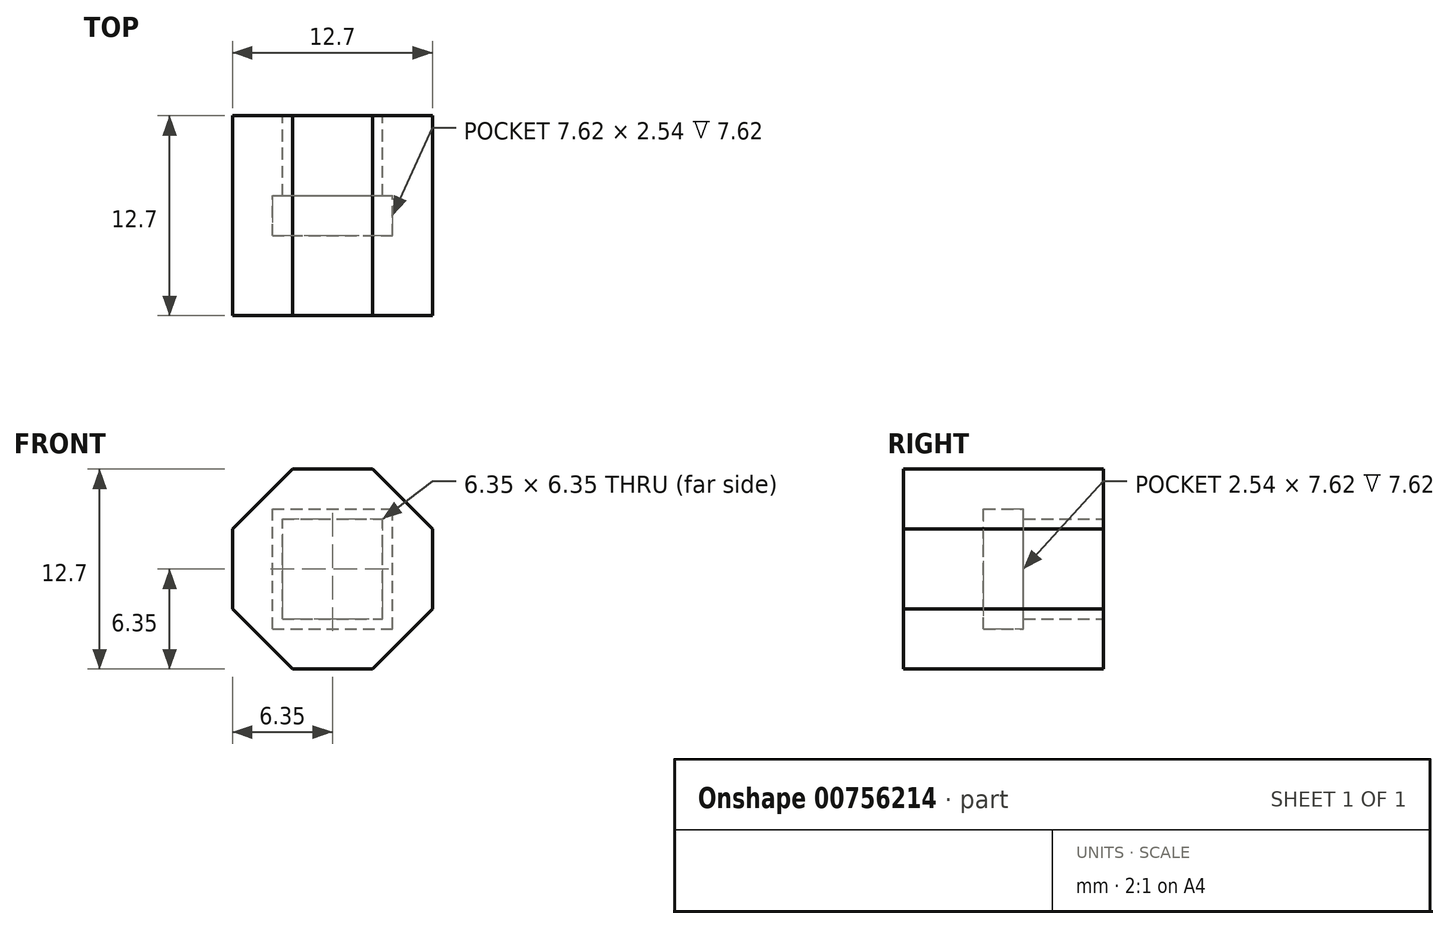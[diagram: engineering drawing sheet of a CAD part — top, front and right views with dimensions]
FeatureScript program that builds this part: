
annotation { "Feature Type Name" : "Feature", "Feature Type Description" : "" }
export const myFeature = defineFeature(function(context is Context, id is Id, definition is map)
    precondition{}
    {
        {
            var Q0;
            Q0=qCreatedBy(makeId("Front.planeOp"),FACE);
            var sketch = newSketch(context, id + "F0", { "sketchPlane" : qUnion([Q0])});
            skLineSegment(sketch, "E0.bottom", {"start": v(-6.35, -6.35) * mm, "end": v(6.35, -6.35) * mm});
            skLineSegment(sketch, "E0.top", {"start": v(-6.35, 6.35) * mm, "end": v(6.35, 6.35) * mm});
            skLineSegment(sketch, "E0.left", {"start": v(-6.35, -6.35) * mm, "end": v(-6.35, 6.35) * mm});
            skLineSegment(sketch, "E0.right", {"start": v(6.35, -6.35) * mm, "end": v(6.35, 6.35) * mm});
            skPoint(sketch, "E0.middle", {"position": v(0, 0) * mm});
            skLineSegment(sketch, "E1.bottom", {"start": v(-3.8, -3.81) * mm, "end": v(3.81, -3.81) * mm});
            skLineSegment(sketch, "E1.top", {"start": v(-3.81, 3.81) * mm, "end": v(3.8, 3.81) * mm});
            skLineSegment(sketch, "E1.left", {"start": v(-3.8, -3.81) * mm, "end": v(-3.81, 3.8) * mm});
            skLineSegment(sketch, "E1.right", {"start": v(3.81, -3.81) * mm, "end": v(3.8, 3.81) * mm});
            skLineSegment(sketch, "E2.bottom", {"start": v(-3.17, -3.18) * mm, "end": v(3.18, -3.18) * mm});
            skLineSegment(sketch, "E2.top", {"start": v(-3.18, 3.18) * mm, "end": v(3.17, 3.18) * mm});
            skLineSegment(sketch, "E2.left", {"start": v(-3.17, -3.18) * mm, "end": v(-3.18, 3.18) * mm});
            skLineSegment(sketch, "E2.right", {"start": v(3.18, -3.18) * mm, "end": v(3.17, 3.18) * mm});
            skSolve(sketch);
        }
        {
            var Q0;
            Q0=qSketchRegion(id+"F0",true);
            var Q1;
            Q1=makeQuery(id+"F0.imprint","IMPRINT",FACE,{"disambiguationData":[TD([[makeQuery(id+"F0.imprint","IMPRINT",EDGE,{"derivedFrom":sQuery(id+"F0.wireOp",EDGE,"E1.bottom")}),1.0]])]});
            var Q2;
            Q2=makeQuery(id+"F0.imprint","IMPRINT",FACE,{"disambiguationData":[TD([[makeQuery(id+"F0.imprint","IMPRINT",EDGE,{"derivedFrom":sQuery(id+"F0.wireOp",EDGE,"E2.bottom")}),1.0]])]});
            extrude(context, id + "F1", {"entities" : qUnion([Q0, Q1, Q2]), "depth" : 12.7 * mm, "offsetDistance" : 25.4 * mm});
        }
        {
            var Q0;
            Q0=makeQuery(id+"F0.imprint","IMPRINT",FACE,{"disambiguationData":[TD([[makeQuery(id+"F0.imprint","IMPRINT",EDGE,{"derivedFrom":sQuery(id+"F0.wireOp",EDGE,"E2.bottom")}),1.0]])]});
            extrude(context, id + "F2", {"entities" : qUnion([Q0]), "operationType" : NewBodyOperationType.REMOVE, "depth" : 7.62 * mm, "offsetDistance" : 25.4 * mm});
        }
        {
            var Q0;
            Q0=makeQuery(id+"F0.imprint","IMPRINT",FACE,{"disambiguationData":[TD([[makeQuery(id+"F0.imprint","IMPRINT",EDGE,{"derivedFrom":sQuery(id+"F0.wireOp",EDGE,"E1.bottom")}),1.0]])]});
            extrude(context, id + "F3", {"entities" : qUnion([Q0]), "operationType" : NewBodyOperationType.REMOVE, "depth" : 7.62 * mm, "offsetDistance" : 25.4 * mm});
        }
        {
            var Q0;
            Q0=makeQuery(id+"F0.imprint","IMPRINT",FACE,{"disambiguationData":[TD([[makeQuery(id+"F0.imprint","IMPRINT",EDGE,{"derivedFrom":sQuery(id+"F0.wireOp",EDGE,"E1.bottom")}),1.0]])]});
            extrude(context, id + "F4", {"entities" : qUnion([Q0]), "operationType" : NewBodyOperationType.ADD, "depth" : 5.08 * mm, "offsetDistance" : 25.4 * mm});
        }
        {
            var Q0;
            Q0=makeQuery(id+"F1.opExtrude","SWEPT_EDGE",EDGE,{"disambiguationData":[OSD([sQuery(id+"F0.wireOp",EDGE,"E0.bottom"),sQuery(id+"F0.wireOp",EDGE,"E0.left")])]});
            var Q1;
            Q1=makeQuery(id+"F1.opExtrude","SWEPT_EDGE",EDGE,{"disambiguationData":[OSD([sQuery(id+"F0.wireOp",EDGE,"E0.bottom"),sQuery(id+"F0.wireOp",EDGE,"E0.right")])]});
            var Q2;
            Q2=makeQuery(id+"F1.opExtrude","SWEPT_EDGE",EDGE,{"disambiguationData":[OSD([sQuery(id+"F0.wireOp",EDGE,"E0.top"),sQuery(id+"F0.wireOp",EDGE,"E0.right")])]});
            var Q3;
            Q3=makeQuery(id+"F1.opExtrude","SWEPT_EDGE",EDGE,{"disambiguationData":[OSD([sQuery(id+"F0.wireOp",EDGE,"E0.top"),sQuery(id+"F0.wireOp",EDGE,"E0.left")])]});
            chamfer(context, id + "F5", {"entities" : qUnion([Q0, Q1, Q2, Q3]), "width" : 3.8 * mm, "tangentPropagation" : true});
        }
    });
